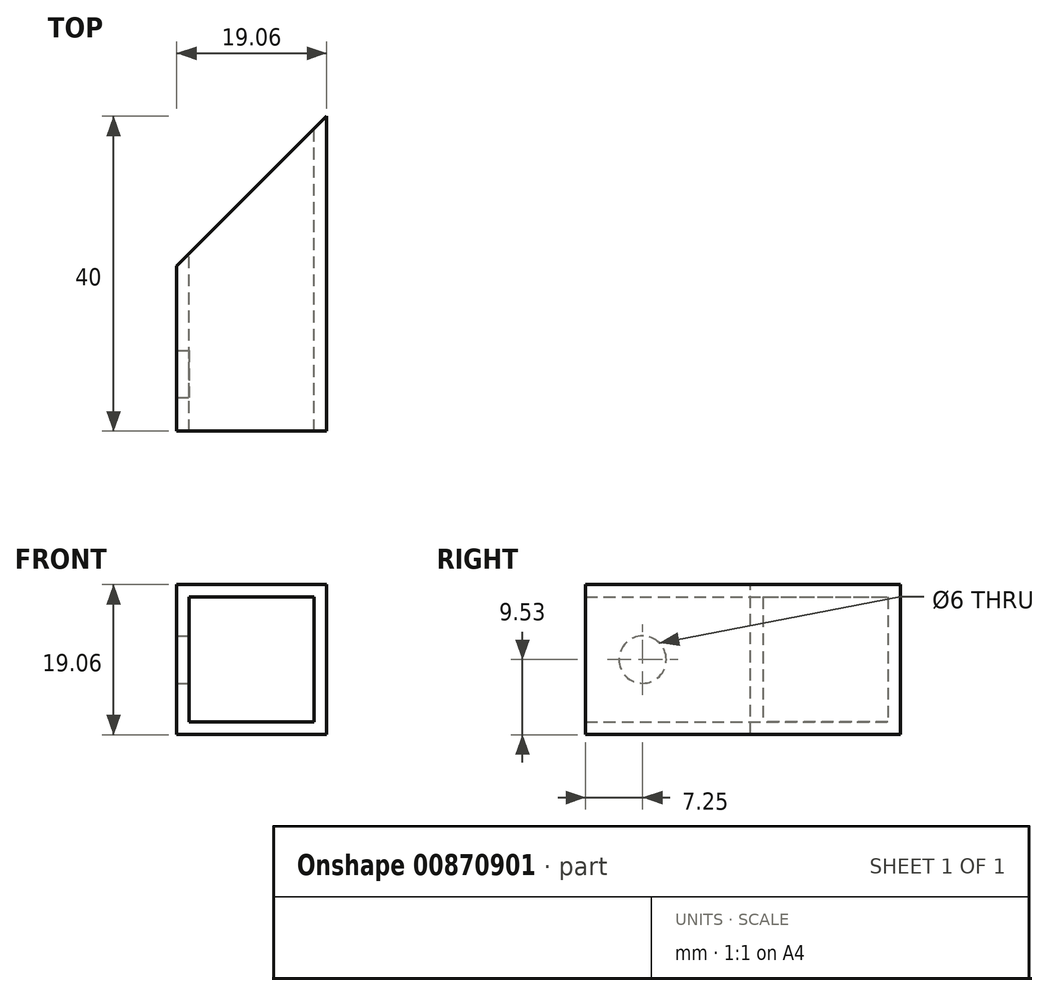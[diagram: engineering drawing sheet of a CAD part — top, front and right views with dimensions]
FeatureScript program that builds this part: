
annotation { "Feature Type Name" : "Feature", "Feature Type Description" : "" }
export const myFeature = defineFeature(function(context is Context, id is Id, definition is map)
    precondition{}
    {
        {
            var Q0;
            Q0=qCreatedBy(makeId("Front.planeOp"),FACE);
            var sketch = newSketch(context, id + "F0", { "sketchPlane" : qUnion([Q0])});
            skLineSegment(sketch, "E0.bottom", {"start": v(9.53, 9.53) * mm, "end": v(-9.53, 9.53) * mm});
            skLineSegment(sketch, "E0.top", {"start": v(9.53, -9.52) * mm, "end": v(-9.53, -9.52) * mm});
            skLineSegment(sketch, "E0.left", {"start": v(9.53, 9.53) * mm, "end": v(9.53, -9.52) * mm});
            skLineSegment(sketch, "E0.right", {"start": v(-9.53, 9.53) * mm, "end": v(-9.53, -9.52) * mm});
            skPoint(sketch, "E0.middle", {"position": v(0, 0) * mm});
            skLineSegment(sketch, "E1.bottom", {"start": v(7.94, 7.94) * mm, "end": v(-7.94, 7.94) * mm});
            skLineSegment(sketch, "E1.top", {"start": v(7.94, -7.94) * mm, "end": v(-7.94, -7.94) * mm});
            skLineSegment(sketch, "E1.left", {"start": v(7.94, 7.94) * mm, "end": v(7.94, -7.94) * mm});
            skLineSegment(sketch, "E1.right", {"start": v(-7.94, 7.94) * mm, "end": v(-7.94, -7.94) * mm});
            skSolve(sketch);
        }
        {
            var Q0;
            Q0=qSketchRegion(id+"F0",true);
            extrude(context, id + "F1", {"entities" : qUnion([Q0]), "depth" : 40 * mm, "offsetDistance" : 25 * mm});
        }
        {
            var Q0;
            Q0=qCreatedBy(makeId("Top.planeOp"),FACE);
            var sketch = newSketch(context, id + "F2", { "sketchPlane" : qUnion([Q0])});
            skLineSegment(sketch, "E2", {"start": v(-9.53, 0) * mm, "end": v(9.53, 0) * mm});
            skLineSegment(sketch, "E3", {"start": v(-9.53, 0) * mm, "end": v(-9.53, -19.05) * mm});
            skLineSegment(sketch, "E4", {"start": v(-9.53, -19.05) * mm, "end": v(9.53, 0) * mm});
            skPoint(sketch, "E5", {"position": v(0, -40) * mm});
            skSolve(sketch);
        }
        {
            var Q0;
            Q0=qSketchRegion(id+"F2",true);
            extrude(context, id + "F3", {"entities" : qUnion([Q0]), "operationType" : NewBodyOperationType.REMOVE, "endBound" : BoundingType.THROUGH_ALL, "oppositeDirection" : true, "depth" : 25 * mm, "offsetDistance" : 25 * mm});
        }
        {
            var Q0;
            Q0=qSketchRegion(id+"F2",true);
            extrude(context, id + "F4", {"entities" : qUnion([Q0]), "operationType" : NewBodyOperationType.REMOVE, "endBound" : BoundingType.THROUGH_ALL, "depth" : 25 * mm, "offsetDistance" : 25 * mm});
        }
        {
            var Q0;
            Q0=qCreatedBy(makeId("Right.planeOp"),FACE);
            var sketch = newSketch(context, id + "F5", { "sketchPlane" : qUnion([Q0])});
            skPoint(sketch, "E6", {"position": v(-32.75, 0) * mm});
            skCircle(sketch, "E7", {"center": v(-32.75, 0) * mm, "radius": 3 * mm});
            skSolve(sketch);
        }
        {
            var Q0;
            Q0 = qSketchRegion(id + "F5", true);
            extrude(context, id + "F6", {"entities" : qUnion([Q0]), "operationType" : NewBodyOperationType.REMOVE, "endBound" : BoundingType.THROUGH_ALL, "oppositeDirection" : true, "depth" : 25 * mm, "offsetDistance" : 25 * mm});
        }
    });
